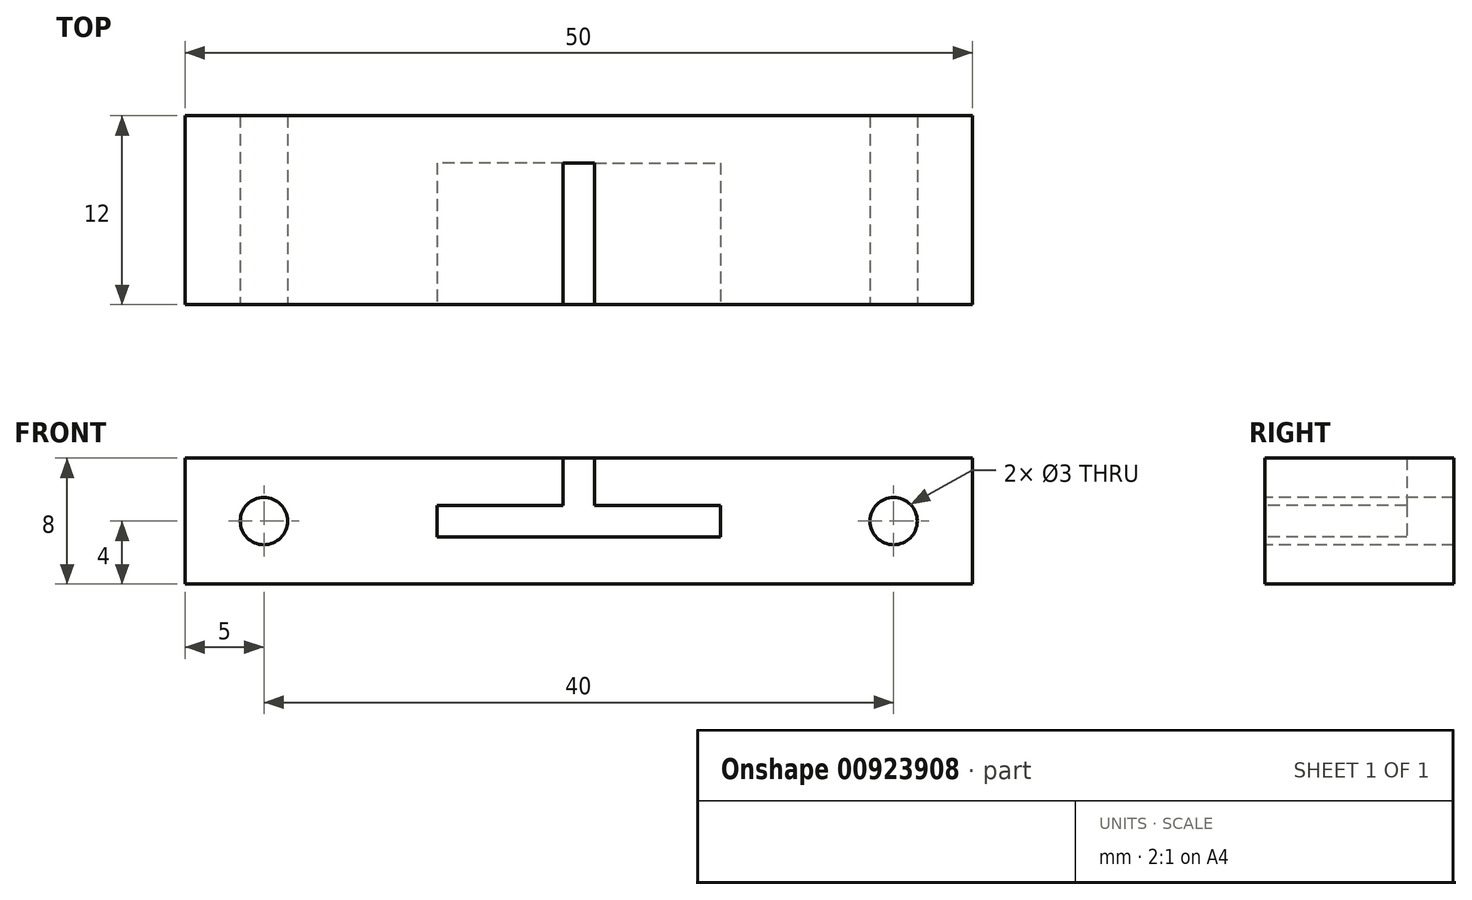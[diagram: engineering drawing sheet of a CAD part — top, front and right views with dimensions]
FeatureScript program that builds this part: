
annotation { "Feature Type Name" : "Feature", "Feature Type Description" : "" }
export const myFeature = defineFeature(function(context is Context, id is Id, definition is map)
    precondition{}
    {
        {
            var Q0;
            Q0=qCreatedBy(makeId("Top.planeOp"),FACE);
            var sketch = newSketch(context, id + "F0", { "sketchPlane" : qUnion([Q0])});
            skLineSegment(sketch, "E0.bottom", {"start": v(0, 0) * mm, "end": v(50, 0) * mm});
            skLineSegment(sketch, "E0.top", {"start": v(0, 12) * mm, "end": v(50, 12) * mm});
            skLineSegment(sketch, "E0.left", {"start": v(0, 0) * mm, "end": v(0, 12) * mm});
            skLineSegment(sketch, "E0.right", {"start": v(50, 0) * mm, "end": v(50, 12) * mm});
            skSolve(sketch);
        }
        {
            var Q0;
            Q0=makeQuery(id+"F0.imprint","IMPRINT",FACE,{"disambiguationData":[TD([[makeQuery(id+"F0.imprint","IMPRINT",EDGE,{"derivedFrom":sQuery(id+"F0.wireOp",EDGE,"E0.bottom")}),1.0]])]});
            extrude(context, id + "F1", {"entities" : qUnion([Q0]), "depth" : 8 * mm, "offsetDistance" : 25 * mm});
        }
        {
            var Q0;
            Q0=makeQuery(id+"F1.opExtrude","SWEPT_FACE",FACE,{"disambiguationData":[OSD([sQuery(id+"F0.wireOp",EDGE,"E0.bottom")])]});
            var sketch = newSketch(context, id + "F2", { "sketchPlane" : qUnion([Q0])});
            skCircle(sketch, "E1", {"center": v(5, 4) * mm, "radius": 1.5 * mm});
            skCircle(sketch, "E2", {"center": v(45, 4) * mm, "radius": 1.5 * mm});
            skLineSegment(sketch, "E3", {"start": v(24, 8) * mm, "end": v(24, 5) * mm});
            skLineSegment(sketch, "E4", {"start": v(24, 5) * mm, "end": v(16, 5) * mm});
            skLineSegment(sketch, "E5", {"start": v(16, 5) * mm, "end": v(16, 3) * mm});
            skLineSegment(sketch, "E6", {"start": v(16, 3) * mm, "end": v(34, 3) * mm});
            skLineSegment(sketch, "E7", {"start": v(34, 3) * mm, "end": v(34, 5) * mm});
            skLineSegment(sketch, "E8", {"start": v(34, 5) * mm, "end": v(26, 5) * mm});
            skLineSegment(sketch, "E9", {"start": v(26, 5) * mm, "end": v(26, 8) * mm});
            skSolve(sketch);
        }
        {
            var Q0;
            Q0=makeQuery(id+"F2.imprint","IMPRINT",FACE,{"disambiguationData":[TD([[makeQuery(id+"F2.imprint","IMPRINT",EDGE,{"derivedFrom":sQuery(id+"F2.wireOp",EDGE,"E1")}),1.0]])]});
            var Q1;
            Q1=makeQuery(id+"F2.imprint","IMPRINT",FACE,{"disambiguationData":[TD([[makeQuery(id+"F2.imprint","IMPRINT",EDGE,{"derivedFrom":sQuery(id+"F2.wireOp",EDGE,"E2")}),1.0]])]});
            extrude(context, id + "F3", {"entities" : qUnion([Q0, Q1]), "operationType" : NewBodyOperationType.REMOVE, "oppositeDirection" : true, "depth" : 12 * mm, "offsetDistance" : 25 * mm});
        }
        {
            var Q0;
            {var subQ0=sQuery(id+"F2.wireOp",EDGE,"E3");Q0=makeQuery(id+"F2.imprint","IMPRINT",FACE,{"disambiguationData":[TD([[makeQuery(id+"F2.imprint","IMPRINT",EDGE,{"derivedFrom":subQ0}),1.0]])]});}
            extrude(context, id + "F4", {"entities" : qUnion([Q0]), "operationType" : NewBodyOperationType.REMOVE, "oppositeDirection" : true, "depth" : 9 * mm, "offsetDistance" : 25 * mm});
        }
    });
